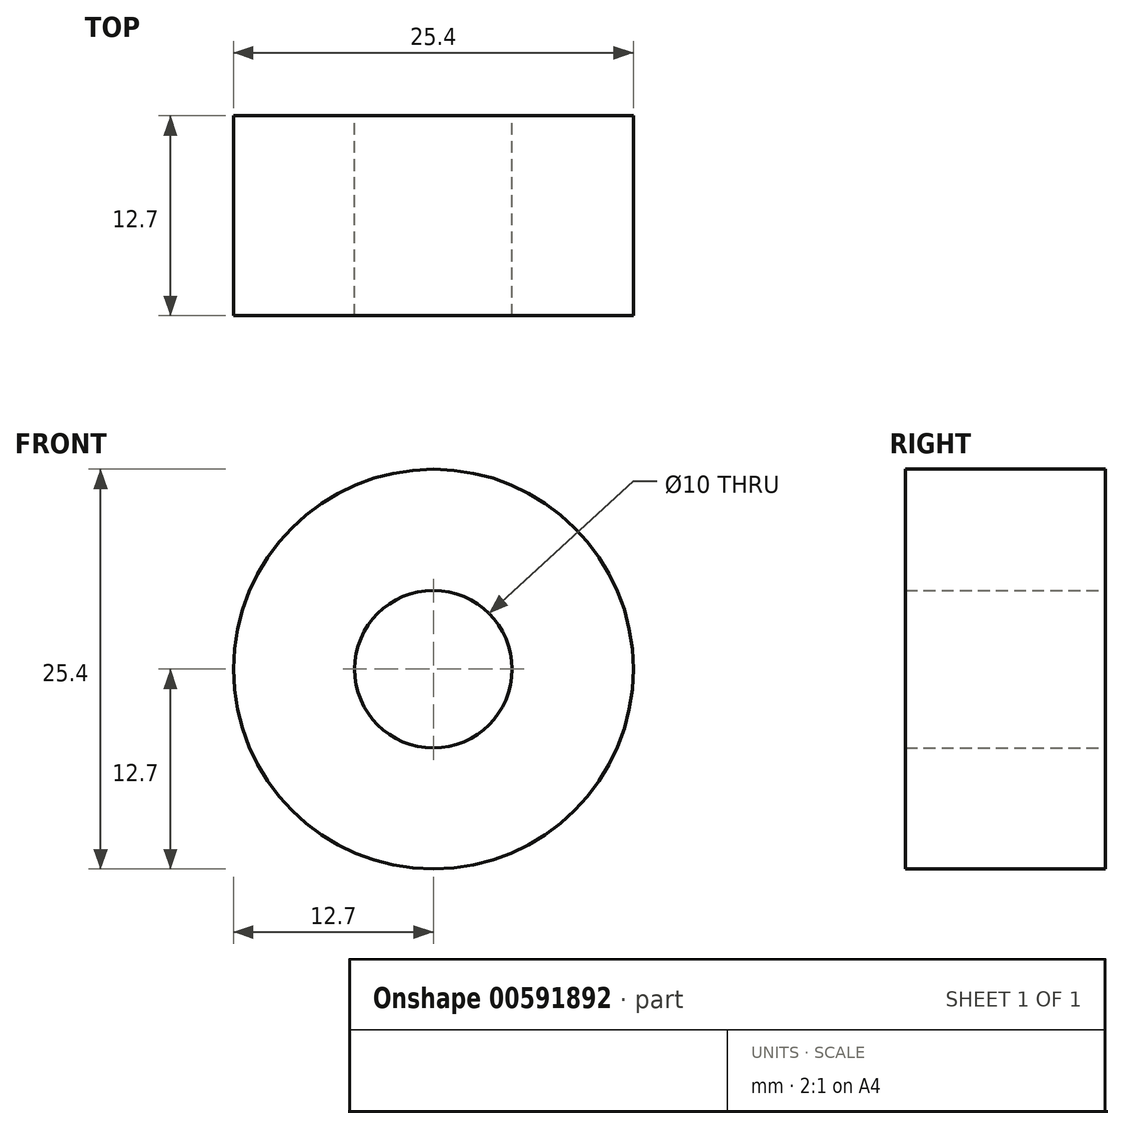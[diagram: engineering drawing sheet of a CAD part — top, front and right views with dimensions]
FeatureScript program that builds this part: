
annotation { "Feature Type Name" : "Feature", "Feature Type Description" : "" }
export const myFeature = defineFeature(function(context is Context, id is Id, definition is map)
    precondition{}
    {
        {
            var Q0;
            Q0=qCreatedBy(makeId("Front.planeOp"),FACE);
            var sketch = newSketch(context, id + "F0", { "sketchPlane" : qUnion([Q0])});
            skCircle(sketch, "E0", {"center": v(0, 0) * mm, "radius": 12.7 * mm});
            skCircle(sketch, "E1", {"center": v(0, 0) * mm, "radius": 5 * mm});
            skSolve(sketch);
        }
        {
            var Q0;
            Q0=makeQuery(id+"F0.imprint","IMPRINT",FACE,{"disambiguationData":[TD([[makeQuery(id+"F0.imprint","IMPRINT",EDGE,{"derivedFrom":sQuery(id+"F0.wireOp",EDGE,"E0")}),1.0]])]});
            extrude(context, id + "F1", {"entities" : qUnion([Q0]), "depth" : 12.7 * mm, "offsetDistance" : 25 * mm});
        }
    });
